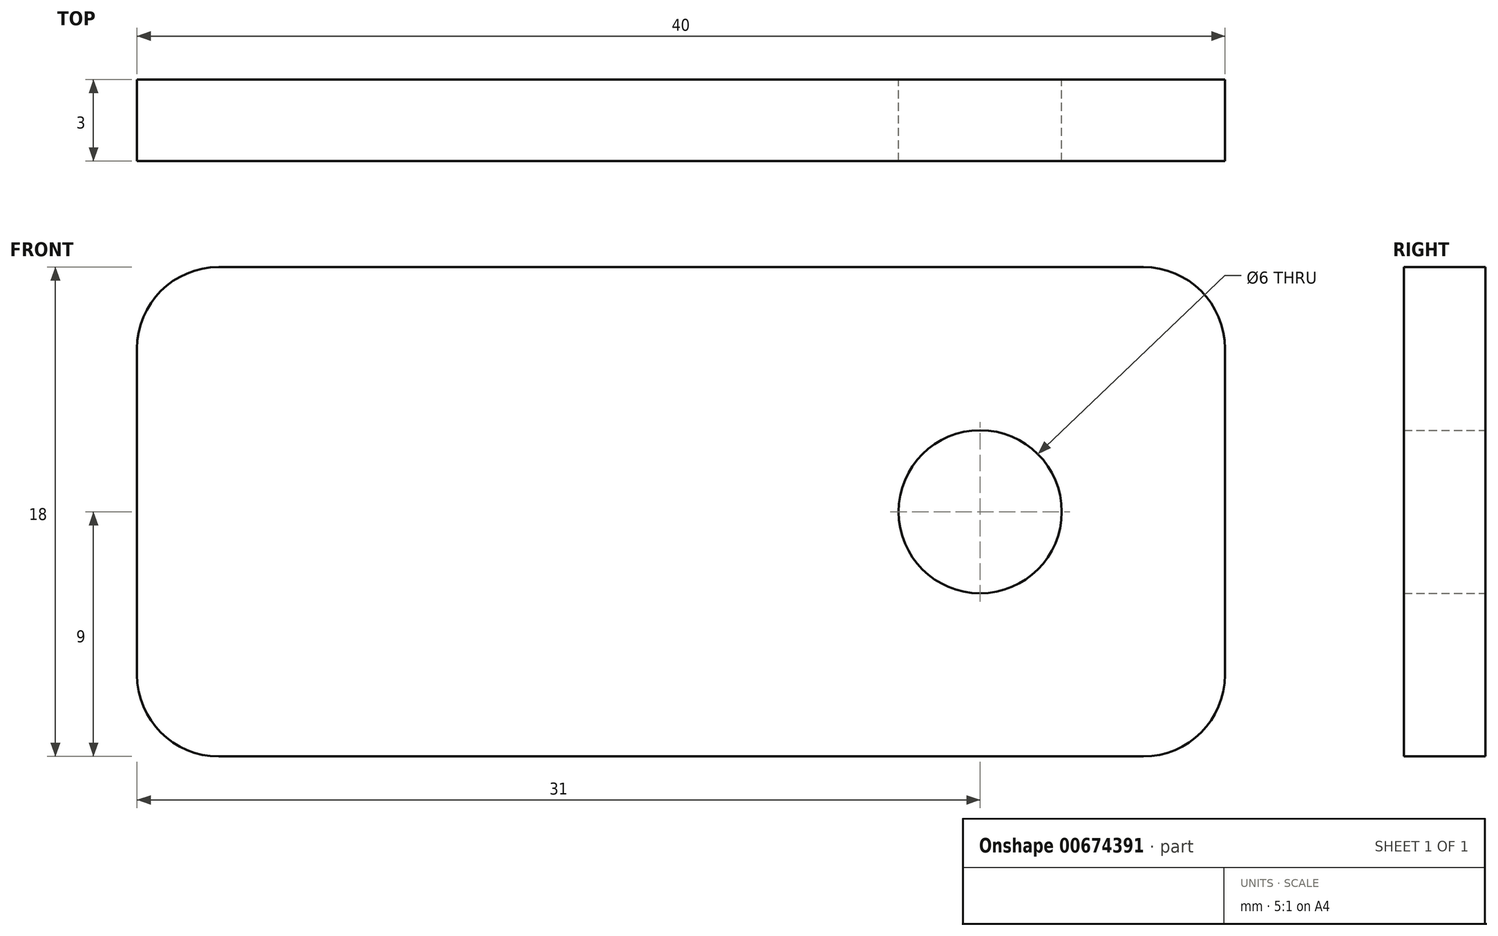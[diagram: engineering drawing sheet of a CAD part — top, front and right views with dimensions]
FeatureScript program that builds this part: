
annotation { "Feature Type Name" : "Feature", "Feature Type Description" : "" }
export const myFeature = defineFeature(function(context is Context, id is Id, definition is map)
    precondition{}
    {
        {
            var Q0;
            Q0=qCreatedBy(makeId("Front.planeOp"),FACE);
            var sketch = newSketch(context, id + "F0", { "sketchPlane" : qUnion([Q0])});
            skLineSegment(sketch, "E0.bottom", {"start": v(17, -9) * mm, "end": v(-17, -9) * mm});
            skLineSegment(sketch, "E0.top", {"start": v(17, 9) * mm, "end": v(-17, 9) * mm});
            skLineSegment(sketch, "E0.left", {"start": v(20, -6) * mm, "end": v(20, 6) * mm});
            skLineSegment(sketch, "E0.right", {"start": v(-20, -6) * mm, "end": v(-20, 6) * mm});
            skPoint(sketch, "E0.middle", {"position": v(0, 0) * mm});
            skCircle(sketch, "E1", {"center": v(11, 0) * mm, "radius": 3 * mm});
            skPoint(sketch, "E2.visualSharp", {"position": v(-20, 9) * mm});
            skArc(sketch, "E2.filletArc", {"start": v(-17, 9) * mm, "mid": v(-19.12, 8.12) * mm, "end": v(-20, 6) * mm});
            skPoint(sketch, "E3.visualSharp", {"position": v(-20, -9) * mm});
            skArc(sketch, "E3.filletArc", {"start": v(-20, -6) * mm, "mid": v(-19.12, -8.12) * mm, "end": v(-17, -9) * mm});
            skPoint(sketch, "E4.visualSharp", {"position": v(20, -9) * mm});
            skArc(sketch, "E4.filletArc", {"start": v(17, -9) * mm, "mid": v(19.12, -8.12) * mm, "end": v(20, -6) * mm});
            skPoint(sketch, "E5.visualSharp", {"position": v(20, 9) * mm});
            skArc(sketch, "E5.filletArc", {"start": v(20, 6) * mm, "mid": v(19.12, 8.12) * mm, "end": v(17, 9) * mm});
            skSolve(sketch);
        }
        {
            var Q0;
            Q0=makeQuery(id+"F0.imprint","IMPRINT",FACE,{"disambiguationData":[TD([[makeQuery(id+"F0.imprint","IMPRINT",EDGE,{"derivedFrom":sQuery(id+"F0.wireOp",EDGE,"E0.bottom")}),-1.0]])]});
            extrude(context, id + "F1", {"entities" : qUnion([Q0]), "depth" : 3 * mm, "offsetDistance" : 25 * mm});
        }
    });
